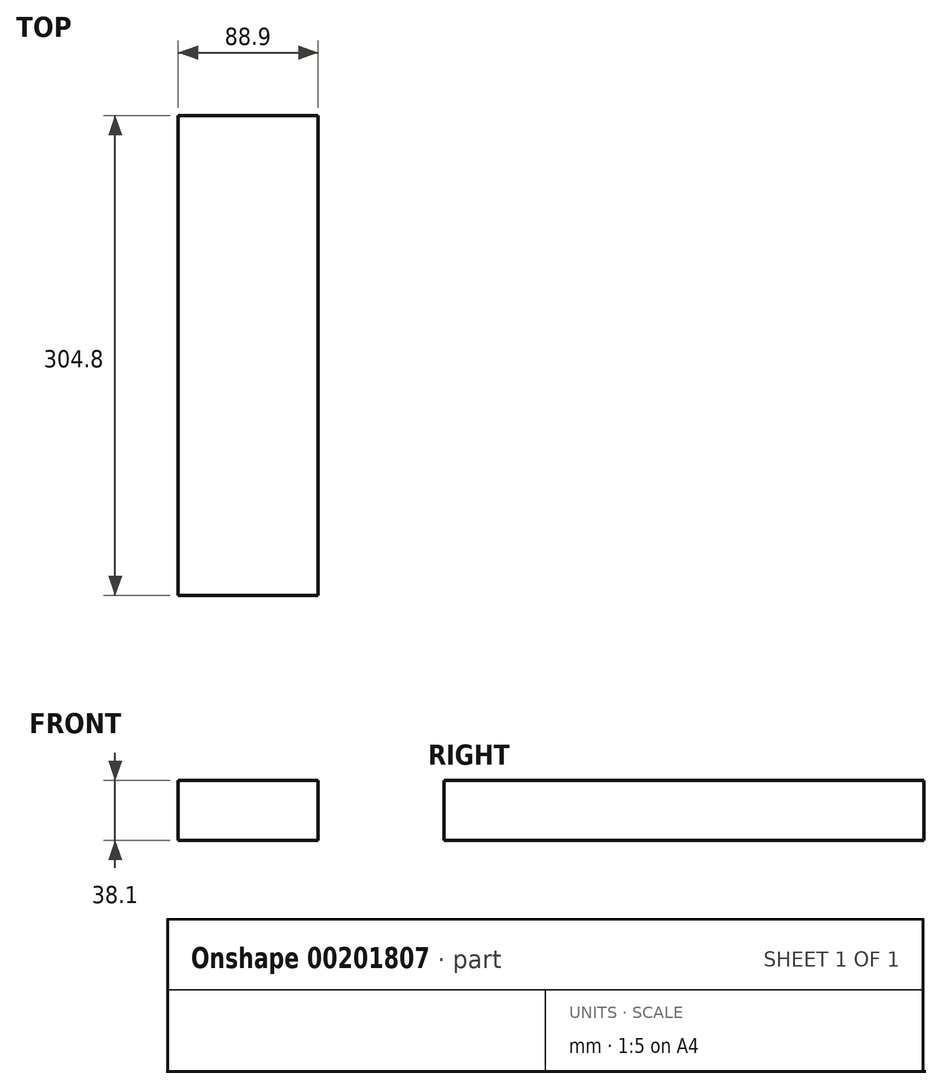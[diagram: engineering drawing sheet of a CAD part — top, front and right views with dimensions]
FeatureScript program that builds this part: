
annotation { "Feature Type Name" : "Feature", "Feature Type Description" : "" }
export const myFeature = defineFeature(function(context is Context, id is Id, definition is map)
    precondition{}
    {
        {
            var Q0;
            Q0=qCreatedBy(makeId("Front.planeOp"),FACE);
            var sketch = newSketch(context, id + "F0", { "sketchPlane" : qUnion([Q0])});
            skLineSegment(sketch, "E0.bottom", {"start": v(44.45, -19.05) * mm, "end": v(-44.45, -19.05) * mm});
            skLineSegment(sketch, "E0.top", {"start": v(44.45, 19.05) * mm, "end": v(-44.45, 19.05) * mm});
            skLineSegment(sketch, "E0.left", {"start": v(44.45, -19.05) * mm, "end": v(44.45, 19.05) * mm});
            skLineSegment(sketch, "E0.right", {"start": v(-44.45, -19.05) * mm, "end": v(-44.45, 19.05) * mm});
            skPoint(sketch, "E0.middle", {"position": v(0, 0) * mm});
            skSolve(sketch);
        }
        {
            var Q0;
            Q0 = qSketchRegion(id + "F0", true);
            extrude(context, id + "F1", {"entities" : qUnion([Q0]), "depth" : 304.8 * mm});
        }
    });
